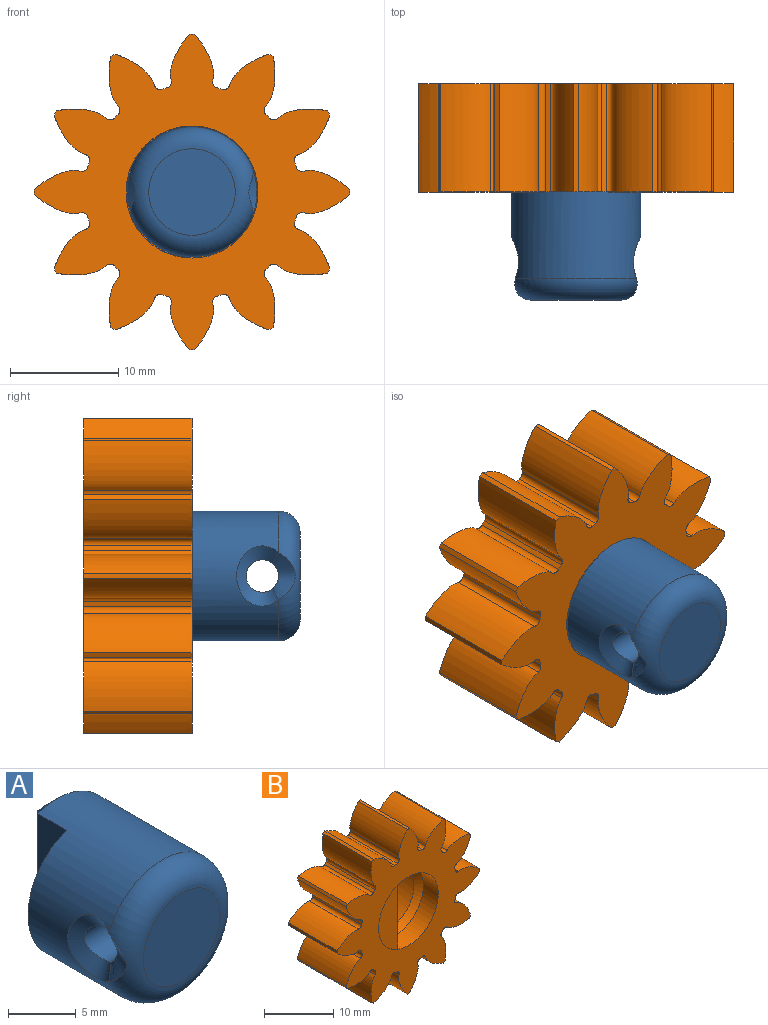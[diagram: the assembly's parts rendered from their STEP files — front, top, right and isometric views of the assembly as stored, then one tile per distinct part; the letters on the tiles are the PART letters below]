
ASSEMBLY  parts=2 mates=1
PART A: 13 faces, bbox 13x14.1x13 mm
  f0: plane 10x6mm, normal (0,1,0), area 49.2mm2, adj f5,f6
  f1: plane 11.31x3mm, normal (-1,0,0), area 33.9mm2, adj f2,f4,f5
  f2: cylinder r=6mm len=12mm, axis (0,-1,0), area 333mm2, adj f1,f4,f6,f7,f9,f11
  f3: plane 8x8mm, normal (0,-1,0), area 50.3mm2, adj f7
  f4: plane 11.31x4mm, normal (0,1,0), area 33mm2, adj f1,f2
  f5: plane 11.37x1.06mm, normal (-0.71,0.71,0), area 15mm2, adj f0,f1,f6
  f6: cone r=6mm half-angle=45deg, axis (0,-1,0), area 28.7mm2, adj f0,f2,f5
  f7: torus R=4mm, axis (0,-1,0), area 93.8mm2, adj f2,f3,f10,f12
  f8: cylinder r=1.5mm len=9.57mm, axis (1,0,0), area 90.2mm2, adj f9,f10,f11,f12
  f9: bspline ~5.65x3.88mm, area 13mm2, adj f2,f8,f10
  f10: bspline ~4.31x2.11mm, area 6.4mm2, adj f7,f8,f9
  f11: bspline ~5.65x3.88mm, area 13mm2, adj f2,f8,f12
  f12: bspline ~4.31x2.11mm, area 6.4mm2, adj f7,f8,f11
PART B: 85 faces, bbox 29.2x10.1x29.2 mm
  f0: cylinder r=14.58mm len=10mm, axis (0,1,0), area 4.7mm2, adj f11,f13,f59,f71
  f1: cylinder r=14.58mm len=10mm, axis (0,1,0), area 4.7mm2, adj f11,f13,f66,f69
  f2: cylinder r=14.58mm len=10mm, axis (0,1,0), area 4.7mm2, adj f11,f13,f54,f61
  f3: cylinder r=14.58mm len=10mm, axis (0,1,0), area 4.7mm2, adj f11,f13,f49,f56
  f4: cylinder r=14.58mm len=10mm, axis (0,1,0), area 4.7mm2, adj f11,f13,f44,f51
  f5: cylinder r=14.58mm len=10mm, axis (0,1,0), area 4.7mm2, adj f11,f13,f34,f46
  f6: cylinder r=14.58mm len=10mm, axis (0,1,0), area 4.7mm2, adj f11,f13,f14,f41
  f7: cylinder r=14.58mm len=10mm, axis (0,1,0), area 4.7mm2, adj f11,f13,f36,f39
  f8: cylinder r=14.58mm len=10mm, axis (0,1,0), area 4.7mm2, adj f11,f13,f24,f31
  f9: cylinder r=14.58mm len=10mm, axis (0,1,0), area 4.7mm2, adj f11,f13,f19,f26
  f10: cylinder r=14.58mm len=10mm, axis (0,1,0), area 4.7mm2, adj f11,f13,f21,f64
  f11: plane 29.17x29.17mm, normal (0,-1,0), area 361.5mm2, adj f0,f1,f2,f3,f4,f5,f6,f7
  f12: cylinder r=14.58mm len=10mm, axis (0,1,0), area 4.7mm2, adj f11,f13,f16,f29
  f13: plane 29.17x29.17mm, normal (0,1,0), area 248.8mm2, adj f0,f1,f2,f3,f4,f5,f6,f7
  f14: extruded ~10x3.62mm, area 48.2mm2, adj f6,f11,f13,f17
  f15: cylinder r=9.9mm len=10mm, axis (0,1,0), area 4.8mm2, adj f11,f13,f17,f18
  f16: extruded ~10x4.33mm, area 48.2mm2, adj f11,f12,f13,f18
  f17: cylinder r=0.55mm len=10mm, axis (0,1,0), area 8.4mm2, adj f11,f13,f14,f15
  f18: cylinder r=0.55mm len=10mm, axis (0,1,0), area 8.4mm2, adj f11,f13,f15,f16
  f19: extruded ~10x3.62mm, area 48.2mm2, adj f9,f11,f13,f22
  f20: cylinder r=9.9mm len=10mm, axis (0,1,0), area 4.8mm2, adj f11,f13,f22,f23
  f21: extruded ~10x4.33mm, area 48.2mm2, adj f10,f11,f13,f23
  f22: cylinder r=0.55mm len=10mm, axis (0,1,0), area 8.4mm2, adj f11,f13,f19,f20
  f23: cylinder r=0.55mm len=10mm, axis (0,1,0), area 8.4mm2, adj f11,f13,f20,f21
  f24: extruded ~10x4.59mm, area 48.2mm2, adj f8,f11,f13,f27
  f25: cylinder r=9.9mm len=10mm, axis (0,1,0), area 4.8mm2, adj f11,f13,f27,f28
  f26: extruded ~10x4.59mm, area 48.2mm2, adj f9,f11,f13,f28
  f27: cylinder r=0.55mm len=10mm, axis (0,1,0), area 8.4mm2, adj f11,f13,f24,f25
  f28: cylinder r=0.55mm len=10mm, axis (0,1,0), area 8.4mm2, adj f11,f13,f25,f26
  f29: extruded ~10x4.33mm, area 48.2mm2, adj f11,f12,f13,f32
  f30: cylinder r=9.9mm len=10mm, axis (0,1,0), area 4.8mm2, adj f11,f13,f32,f33
  f31: extruded ~10x3.62mm, area 48.2mm2, adj f8,f11,f13,f33
  f32: cylinder r=0.55mm len=10mm, axis (0,1,0), area 8.4mm2, adj f11,f13,f29,f30
  f33: cylinder r=0.55mm len=10mm, axis (0,1,0), area 8.4mm2, adj f11,f13,f30,f31
  f34: extruded ~10x4.33mm, area 48.2mm2, adj f5,f11,f13,f37
  f35: cylinder r=9.9mm len=10mm, axis (0,1,0), area 4.8mm2, adj f11,f13,f37,f38
  f36: extruded ~10x3.62mm, area 48.2mm2, adj f7,f11,f13,f38
  f37: cylinder r=0.55mm len=10mm, axis (0,1,0), area 8.4mm2, adj f11,f13,f34,f35
  f38: cylinder r=0.55mm len=10mm, axis (0,1,0), area 8.4mm2, adj f11,f13,f35,f36
  f39: extruded ~10x4.59mm, area 48.2mm2, adj f7,f11,f13,f42
  f40: cylinder r=9.9mm len=10mm, axis (0,1,0), area 4.8mm2, adj f11,f13,f42,f43
  f41: extruded ~10x4.59mm, area 48.2mm2, adj f6,f11,f13,f43
  f42: cylinder r=0.55mm len=10mm, axis (0,1,0), area 8.4mm2, adj f11,f13,f39,f40
  f43: cylinder r=0.55mm len=10mm, axis (0,1,0), area 8.4mm2, adj f11,f13,f40,f41
  f44: extruded ~10x3.62mm, area 48.2mm2, adj f4,f11,f13,f47
  f45: cylinder r=9.9mm len=10mm, axis (0,1,0), area 4.8mm2, adj f11,f13,f47,f48
  f46: extruded ~10x4.33mm, area 48.2mm2, adj f5,f11,f13,f48
  f47: cylinder r=0.55mm len=10mm, axis (0,1,0), area 8.4mm2, adj f11,f13,f44,f45
  f48: cylinder r=0.55mm len=10mm, axis (0,1,0), area 8.4mm2, adj f11,f13,f45,f46
  f49: extruded ~10x4.59mm, area 48.2mm2, adj f3,f11,f13,f52
  f50: cylinder r=9.9mm len=10mm, axis (0,1,0), area 4.8mm2, adj f11,f13,f52,f53
  f51: extruded ~10x4.59mm, area 48.2mm2, adj f4,f11,f13,f53
  f52: cylinder r=0.55mm len=10mm, axis (0,1,0), area 8.4mm2, adj f11,f13,f49,f50
  f53: cylinder r=0.55mm len=10mm, axis (0,1,0), area 8.4mm2, adj f11,f13,f50,f51
  f54: extruded ~10x4.33mm, area 48.2mm2, adj f2,f11,f13,f57
  f55: cylinder r=9.9mm len=10mm, axis (0,1,0), area 4.8mm2, adj f11,f13,f57,f58
  f56: extruded ~10x3.62mm, area 48.2mm2, adj f3,f11,f13,f58
  f57: cylinder r=0.55mm len=10mm, axis (0,1,0), area 8.4mm2, adj f11,f13,f54,f55
  f58: cylinder r=0.55mm len=10mm, axis (0,1,0), area 8.4mm2, adj f11,f13,f55,f56
  f59: extruded ~10x3.62mm, area 48.2mm2, adj f0,f11,f13,f62
  f60: cylinder r=9.9mm len=10mm, axis (0,1,0), area 4.8mm2, adj f11,f13,f62,f63
  f61: extruded ~10x4.33mm, area 48.2mm2, adj f2,f11,f13,f63
  f62: cylinder r=0.55mm len=10mm, axis (0,1,0), area 8.4mm2, adj f11,f13,f59,f60
  f63: cylinder r=0.55mm len=10mm, axis (0,1,0), area 8.4mm2, adj f11,f13,f60,f61
  f64: extruded ~10x4.33mm, area 48.2mm2, adj f10,f11,f13,f67
  f65: cylinder r=9.9mm len=10mm, axis (0,1,0), area 4.8mm2, adj f11,f13,f67,f68
  f66: extruded ~10x3.62mm, area 48.2mm2, adj f1,f11,f13,f68
  f67: cylinder r=0.55mm len=10mm, axis (0,1,0), area 8.4mm2, adj f11,f13,f64,f65
  f68: cylinder r=0.55mm len=10mm, axis (0,1,0), area 8.4mm2, adj f11,f13,f65,f66
  f69: extruded ~10x4.59mm, area 48.2mm2, adj f1,f11,f13,f72
  f70: cylinder r=9.9mm len=10mm, axis (0,1,0), area 4.8mm2, adj f11,f13,f72,f73
  f71: extruded ~10x4.59mm, area 48.2mm2, adj f0,f11,f13,f73
  f72: cylinder r=0.55mm len=10mm, axis (0,1,0), area 8.4mm2, adj f11,f13,f69,f70
  f73: cylinder r=0.55mm len=10mm, axis (0,1,0), area 8.4mm2, adj f11,f13,f70,f71
  f74: cylinder r=8.05mm len=16.1mm, axis (0,1,0), area 227.6mm2, adj f75,f78
  f75: plane 16.1x16.1mm, normal (0,1,0), area 24.5mm2, adj f74,f79
  f76: plane 14.1x14.1mm, normal (0,1,0), area 103mm2, adj f77,f83,f84
  f77: cylinder r=7.05mm len=14.1mm, axis (0,1,0), area 22.1mm2, adj f76,f79
  f78: cone r=8.05mm half-angle=45deg, axis (0,1,0), area 36.9mm2, adj f13,f74
  f79: cone r=7.05mm half-angle=45deg, axis (0,1,0), area 32.4mm2, adj f75,f77
  f80: plane 11.45x2.94mm, normal (1,0,0), area 33.7mm2, adj f81,f82,f83
  f81: cylinder r=6.1mm len=12.2mm, axis (0,-1,0), area 72.8mm2, adj f11,f80,f82,f84
  f82: plane 11.45x4mm, normal (0,-1,0), area 33.3mm2, adj f80,f81
  f83: plane 11.51x1.01mm, normal (0.71,-0.71,0), area 14.6mm2, adj f76,f80,f84
  f84: cone r=6.07mm half-angle=45deg, axis (0,-1,0), area 28.3mm2, adj f76,f81,f83
PLACE A at identity
PLACE B at identity
MATE fastened A.f2 <-> B.f81  axis (0,1,0) through (0,-6,50)mm
